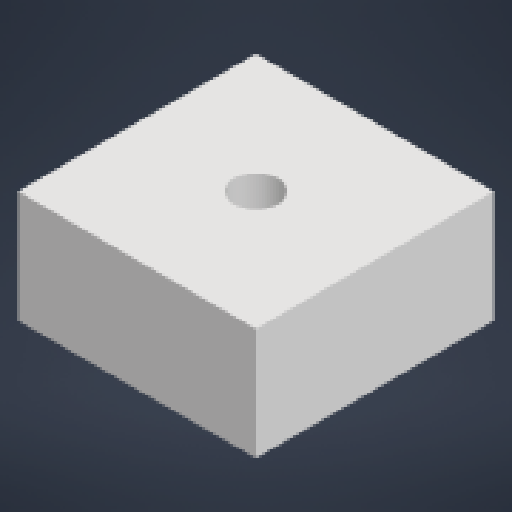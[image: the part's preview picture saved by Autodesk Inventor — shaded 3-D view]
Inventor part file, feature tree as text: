
AUTODESK INVENTOR PART (.ipt)
format: ipt  version: 2023 (Build 270158000, 158)  size: 136,192 bytes
history: native  units: in
note: dims shown in document units (in); Inventor stores cm internally (conversion verified against a paired STEP export)
features: sketch x2, extrude x1, hole x1
ambient origin geometry x8: Origin, YZ Plane, XZ Plane, XY Plane, X Axis, Y Axis, Z Axis, Center Point
bodies: Solid1 (feature_tree)
feature tree (4):
  extrude  "Extrusion1"  Depth=1.0in
  hole  "Hole3"  [1 undecoded]
  sketch  "Sketch1"  dims[d0=9.0in d1=1.0in]
  sketch  "Sketch4"  dims[d2=0.47in d3=0.0in d33=0.1875in d34=0.75in d35=0.375in d36=0.25in d37=0.5635in d38=1.0in d39=0.8108in d40=0.5in d42=0.1875in]
note: 1 required parameter value undecoded (feature->parameter linkage not recoverable at this tier; creation-order binding heuristic only, values carry confidence <= 0.55)
